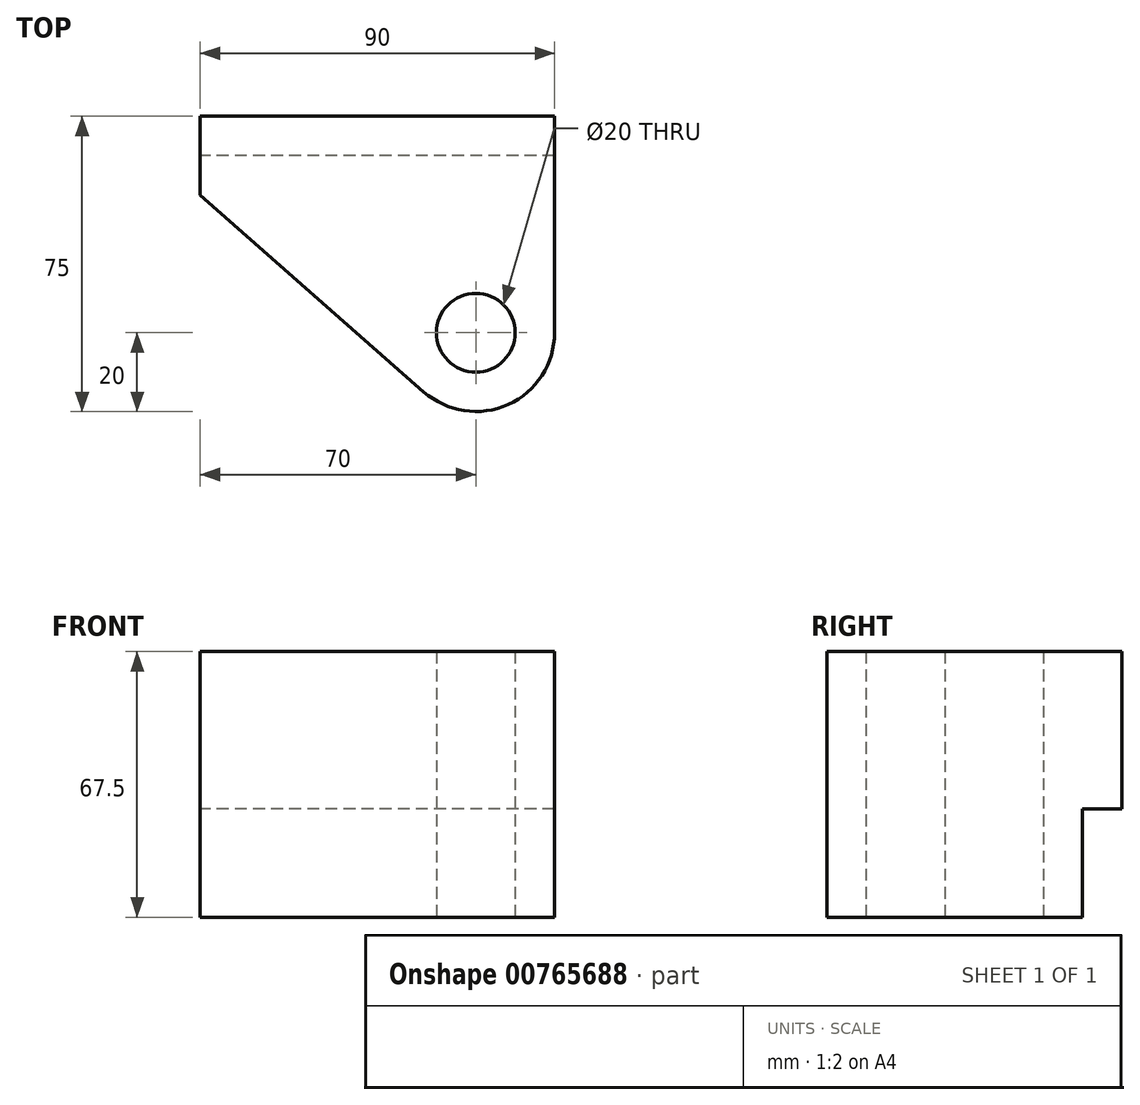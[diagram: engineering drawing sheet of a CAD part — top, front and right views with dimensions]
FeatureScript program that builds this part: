
annotation { "Feature Type Name" : "Feature", "Feature Type Description" : "" }
export const myFeature = defineFeature(function(context is Context, id is Id, definition is map)
    precondition{}
    {
        {
            var Q0;
            Q0=qCreatedBy(makeId("Top.planeOp"),FACE);
            var sketch = newSketch(context, id + "F0", { "sketchPlane" : qUnion([Q0])});
            skLineSegment(sketch, "E0.bottom", {"start": v(45, 37.5) * mm, "end": v(-45, 37.5) * mm});
            skLineSegment(sketch, "E0.left", {"start": v(45, 37.5) * mm, "end": v(45, -17.5) * mm});
            skLineSegment(sketch, "E0.right", {"start": v(-45, 37.5) * mm, "end": v(-45, 17.5) * mm});
            skPoint(sketch, "E0.middle", {"position": v(0, 0) * mm});
            skLineSegment(sketch, "E1", {"start": v(-45, 27.5) * mm, "end": v(45, 27.5) * mm});
            skLineSegment(sketch, "E2", {"start": v(-45, 17.5) * mm, "end": v(45, 17.5) * mm});
            skCircle(sketch, "E3", {"center": v(25, -17.5) * mm, "radius": 20 * mm});
            skLineSegment(sketch, "E4", {"start": v(5, 17.5) * mm, "end": v(5, -17.5) * mm});
            skLineSegment(sketch, "E5", {"start": v(-45, 17.5) * mm, "end": v(12.7, -33.32) * mm});
            skLineSegment(sketch, "E6", {"start": v(-8, 27.5) * mm, "end": v(-8, 17.5) * mm});
            skLineSegment(sketch, "E7", {"start": v(-2, 27.5) * mm, "end": v(-2, 17.5) * mm});
            skCircle(sketch, "E8", {"center": v(25, -17.5) * mm, "radius": 10 * mm});
            skSolve(sketch);
        }
        {
            var Q0;
            {var subQ1=sQuery(id+"F0.wireOp",EDGE,"E0.bottom");Q0=makeQuery(id+"F0.imprint","IMPRINT",FACE,{"disambiguationData":[TD([[makeQuery(id+"F0.imprint","IMPRINT",EDGE,{"derivedFrom":subQ1}),1.0]])]});}
            var Q1;
            {var subQ5=sQuery(id+"F0.wireOp",EDGE,"E6");Q1=makeQuery(id+"F0.imprint","IMPRINT",FACE,{"disambiguationData":[TD([[makeQuery(id+"F0.imprint","IMPRINT",EDGE,{"derivedFrom":subQ5}),-1.0]])]});}
            var Q2;
            {var subQ0=sQuery(id+"F0.wireOp",EDGE,"E6");Q2=makeQuery(id+"F0.imprint","IMPRINT",FACE,{"disambiguationData":[TD([[makeQuery(id+"F0.imprint","IMPRINT",EDGE,{"derivedFrom":subQ0}),1.0]])]});}
            var Q3;
            {var subQ2=sQuery(id+"F0.wireOp",EDGE,"E7");Q3=makeQuery(id+"F0.imprint","IMPRINT",FACE,{"disambiguationData":[TD([[makeQuery(id+"F0.imprint","IMPRINT",EDGE,{"derivedFrom":subQ2}),1.0]])]});}
            var Q4;
            {var subQ0=sQuery(id+"F0.wireOp",EDGE,"E4");Q4=makeQuery(id+"F0.imprint","IMPRINT",FACE,{"disambiguationData":[TD([[makeQuery(id+"F0.imprint","IMPRINT",EDGE,{"derivedFrom":subQ0}),-1.0]])]});}
            var Q5;
            {var subQ5=sQuery(id+"F0.wireOp",EDGE,"E4");Q5=makeQuery(id+"F0.imprint","IMPRINT",FACE,{"disambiguationData":[TD([[makeQuery(id+"F0.imprint","IMPRINT",EDGE,{"derivedFrom":subQ5}),1.0]])]});}
            var Q6;
            Q6=makeQuery(id+"F0.imprint","IMPRINT",FACE,{"disambiguationData":[TD([[makeQuery(id+"F0.imprint","IMPRINT",EDGE,{"derivedFrom":sQuery(id+"F0.wireOp",EDGE,"E8")}),-1.0]])]});
            extrude(context, id + "F1", {"entities" : qUnion([Q0, Q1, Q2, Q3, Q4, Q5, Q6]), "depth" : (135 / 2) * mm, "offsetDistance" : 25 * mm});
        }
        {
            var Q0;
            Q0=makeQuery(id+"F1.opExtrude","SWEPT_FACE",FACE,{"disambiguationData":[OSD([sQuery(id+"F0.wireOp",EDGE,"E0.right")])]});
            var sketch = newSketch(context, id + "F2", { "sketchPlane" : qUnion([Q0])});
            skLineSegment(sketch, "E9.bottom", {"start": v(-37.5, 0) * mm, "end": v(-27.5, 0) * mm});
            skLineSegment(sketch, "E9.top", {"start": v(-37.5, 27.5) * mm, "end": v(-27.5, 27.5) * mm});
            skLineSegment(sketch, "E9.left", {"start": v(-37.5, 0) * mm, "end": v(-37.5, 27.5) * mm});
            skLineSegment(sketch, "E9.right", {"start": v(-27.5, 0) * mm, "end": v(-27.5, 27.5) * mm});
            skSolve(sketch);
        }
        {
            var Q0;
            Q0=makeQuery(id+"F2.imprint","IMPRINT",FACE,{"disambiguationData":[TD([[makeQuery(id+"F2.imprint","IMPRINT",EDGE,{"derivedFrom":sQuery(id+"F2.wireOp",EDGE,"E9.bottom")}),1.0]])]});
            extrude(context, id + "F3", {"entities" : qUnion([Q0]), "operationType" : NewBodyOperationType.REMOVE, "oppositeDirection" : true, "depth" : 250 * mm, "offsetDistance" : 25 * mm});
        }
    });
